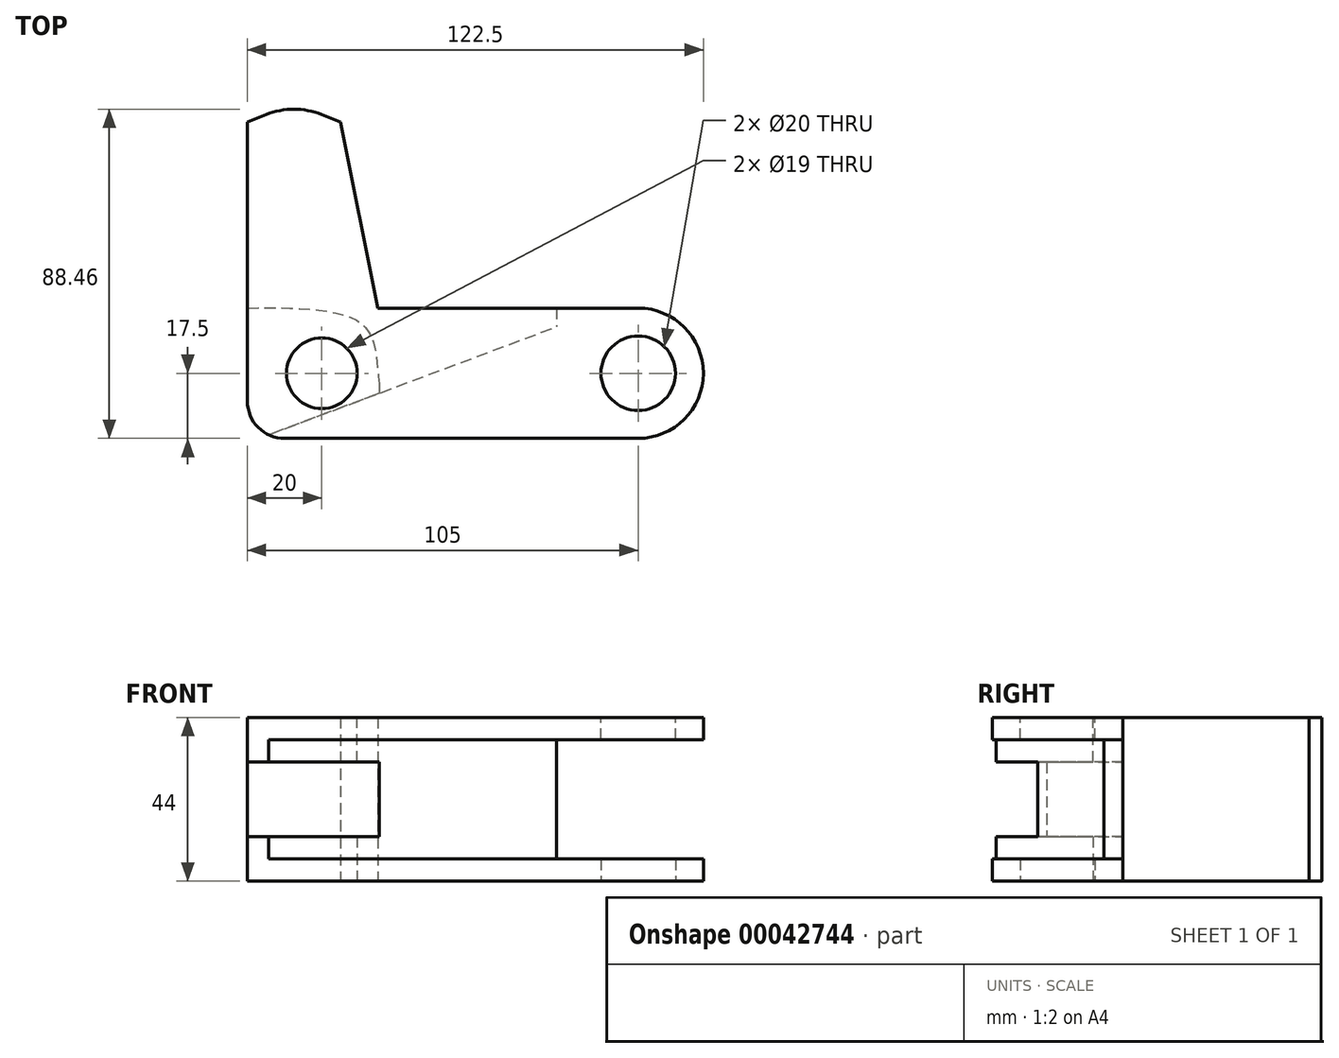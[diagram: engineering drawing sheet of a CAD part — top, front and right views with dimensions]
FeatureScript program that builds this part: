
annotation { "Feature Type Name" : "Feature", "Feature Type Description" : "" }
export const myFeature = defineFeature(function(context is Context, id is Id, definition is map)
    precondition{}
    {
        {
            var Q0;
            Q0=qCreatedBy(makeId("Top.planeOp"),FACE);
            var sketch = newSketch(context, id + "F0", { "sketchPlane" : qUnion([Q0])});
            skCircle(sketch, "E0", {"center": v(0, 0) * mm, "radius": 10 * mm});
            skArc(sketch, "E1", {"start": v(0, -17.5) * mm, "mid": v(17.5, 0) * mm, "end": v(0, 17.5) * mm});
            skLineSegment(sketch, "E2", {"start": v(0, 17.5) * mm, "end": v(-70, 17.5) * mm});
            skLineSegment(sketch, "E3", {"start": v(0, -17.5) * mm, "end": v(-95, -17.5) * mm});
            skCircle(sketch, "E4", {"center": v(-85, 0) * mm, "radius": 9.5 * mm});
            skLineSegment(sketch, "E5", {"start": v(-105, -7.5) * mm, "end": v(-105, 67.5) * mm});
            skLineSegment(sketch, "E6", {"start": v(-105, 67.5) * mm, "end": v(-80, 67.5) * mm});
            skLineSegment(sketch, "E7", {"start": v(-70, 17.5) * mm, "end": v(-80, 67.5) * mm});
            skLineSegment(sketch, "E8", {"start": v(-105, 67.5) * mm, "end": v(-99.93, 69.53) * mm});
            skPoint(sketch, "E8.endSnap0", {"position": v(-92.5, 67.5) * mm});
            skLineSegment(sketch, "E9", {"start": v(-85.07, 69.53) * mm, "end": v(-80, 67.5) * mm});
            skPoint(sketch, "E10.visualSharp", {"position": v(-92.5, 72.5) * mm});
            skArc(sketch, "E10.filletArc", {"start": v(-85.07, 69.53) * mm, "mid": v(-92.5, 70.96) * mm, "end": v(-99.93, 69.53) * mm});
            skPoint(sketch, "E11.visualSharp", {"position": v(-105, -17.5) * mm});
            skArc(sketch, "E11.filletArc", {"start": v(-105, -7.5) * mm, "mid": v(-102.07, -14.57) * mm, "end": v(-95, -17.5) * mm});
            skPoint(sketch, "E12", {"position": v(-22, 17.5) * mm});
            skPoint(sketch, "E13", {"position": v(-105, 17.5) * mm});
            skPoint(sketch, "E14", {"position": v(-69.57, -2.88) * mm});
            skPoint(sketch, "E15", {"position": v(-22, 12.5) * mm});
            skLineSegment(sketch, "E16", {"start": v(-22, 12.5) * mm, "end": v(-22, 17.5) * mm});
            skPoint(sketch, "E17", {"position": v(-73.9, 12.94) * mm});
            skFitSpline(sketch, "E18", {"points": [v(-105, 17.5) * mm, v(-73.9, 12.94) * mm, v(-69.57, -2.88) * mm], "startDerivative": vector(66.56, 1.07) * mm, "endDerivative": vector(5.9, -47.65) * mm});
            skLineSegment(sketch, "E19", {"start": v(-22, 12.5) * mm, "end": v(-99.28, -16.54) * mm});
            skLineSegment(sketch, "E20", {"start": v(-99.28, -16.54) * mm, "end": v(-69.57, -5.38) * mm});
            skLineSegment(sketch, "E21", {"start": v(-69.57, -5.38) * mm, "end": v(-69.57, -2.88) * mm});
            skSolve(sketch);
        }
        {
            var Q0;
            Q0 = qSketchRegion(id + "F0", true);
            extrude(context, id + "F1", {"entities" : qUnion([Q0]), "depth" : 6 * mm});
        }
        {
            var Q0;
            Q0=makeQuery(id+"F0.imprint","IMPRINT",FACE,{"disambiguationData":[TD([[makeQuery(id+"F0.imprint","IMPRINT",EDGE,{"derivedFrom":sQuery(id+"F0.wireOp",EDGE,"E4")}),-1.0]])]});
            var Q1;
            {var subQ5=sQuery(id+"F0.wireOp",EDGE,"E6");Q1=makeQuery(id+"F0.imprint","IMPRINT",FACE,{"disambiguationData":[TD([[makeQuery(id+"F0.imprint","IMPRINT",EDGE,{"derivedFrom":subQ5}),-1.0]])]});}
            var Q2;
            Q2=makeQuery(id+"F0.imprint","IMPRINT",FACE,{"disambiguationData":[TD([[makeQuery(id+"F0.imprint","IMPRINT",EDGE,{"derivedFrom":sQuery(id+"F0.wireOp",EDGE,"E6")}),1.0]])]});
            extrude(context, id + "F2", {"entities" : qUnion([Q0, Q1, Q2]), "operationType" : NewBodyOperationType.ADD, "depth" : 12 * mm});
        }
        {
            var Q0;
            {var subQ5=sQuery(id+"F0.wireOp",EDGE,"E6");Q0=makeQuery(id+"F0.imprint","IMPRINT",FACE,{"disambiguationData":[TD([[makeQuery(id+"F0.imprint","IMPRINT",EDGE,{"derivedFrom":subQ5}),-1.0]])]});}
            var Q1;
            Q1=makeQuery(id+"F0.imprint","IMPRINT",FACE,{"disambiguationData":[TD([[makeQuery(id+"F0.imprint","IMPRINT",EDGE,{"derivedFrom":sQuery(id+"F0.wireOp",EDGE,"E6")}),1.0]])]});
            extrude(context, id + "F3", {"entities" : qUnion([Q0, Q1]), "operationType" : NewBodyOperationType.ADD, "depth" : 22 * mm});
        }
        {
            var Q0;
            Q0=makeQuery(id+"F1.opExtrude","SWEPT_BODY",BODY,{"disambiguationData":[OSD([sQuery(id+"F0.wireOp",EDGE,"E0"),sQuery(id+"F0.wireOp",EDGE,"E1"),sQuery(id+"F0.wireOp",EDGE,"E2"),sQuery(id+"F0.wireOp",EDGE,"E3"),sQuery(id+"F0.wireOp",EDGE,"E4"),sQuery(id+"F0.wireOp",EDGE,"E5"),sQuery(id+"F0.wireOp",EDGE,"E7"),sQuery(id+"F0.wireOp",EDGE,"E8"),sQuery(id+"F0.wireOp",EDGE,"E9"),sQuery(id+"F0.wireOp",EDGE,"E10.filletArc"),sQuery(id+"F0.wireOp",EDGE,"E11.filletArc")])]});
            var Q1;
            Q1=makeQuery(id+"F3.opExtrude","CAP_FACE",FACE,{"disambiguationData":[OSD([sQuery(id+"F0.wireOp",EDGE,"E2"),sQuery(id+"F0.wireOp",EDGE,"E5"),sQuery(id+"F0.wireOp",EDGE,"E7"),sQuery(id+"F0.wireOp",EDGE,"E8"),sQuery(id+"F0.wireOp",EDGE,"E9"),sQuery(id+"F0.wireOp",EDGE,"E10.filletArc"),sQuery(id+"F0.wireOp",EDGE,"E16"),sQuery(id+"F0.wireOp",EDGE,"E18"),sQuery(id+"F0.wireOp",EDGE,"E19"),sQuery(id+"F0.wireOp",EDGE,"E21")])],"isStart":false});
            mirror(context, id + "F4", {"operationType" : NewBodyOperationType.ADD, "entities" : qUnion([Q0]), "mirrorPlane" : qUnion([Q1])});
        }
    });
